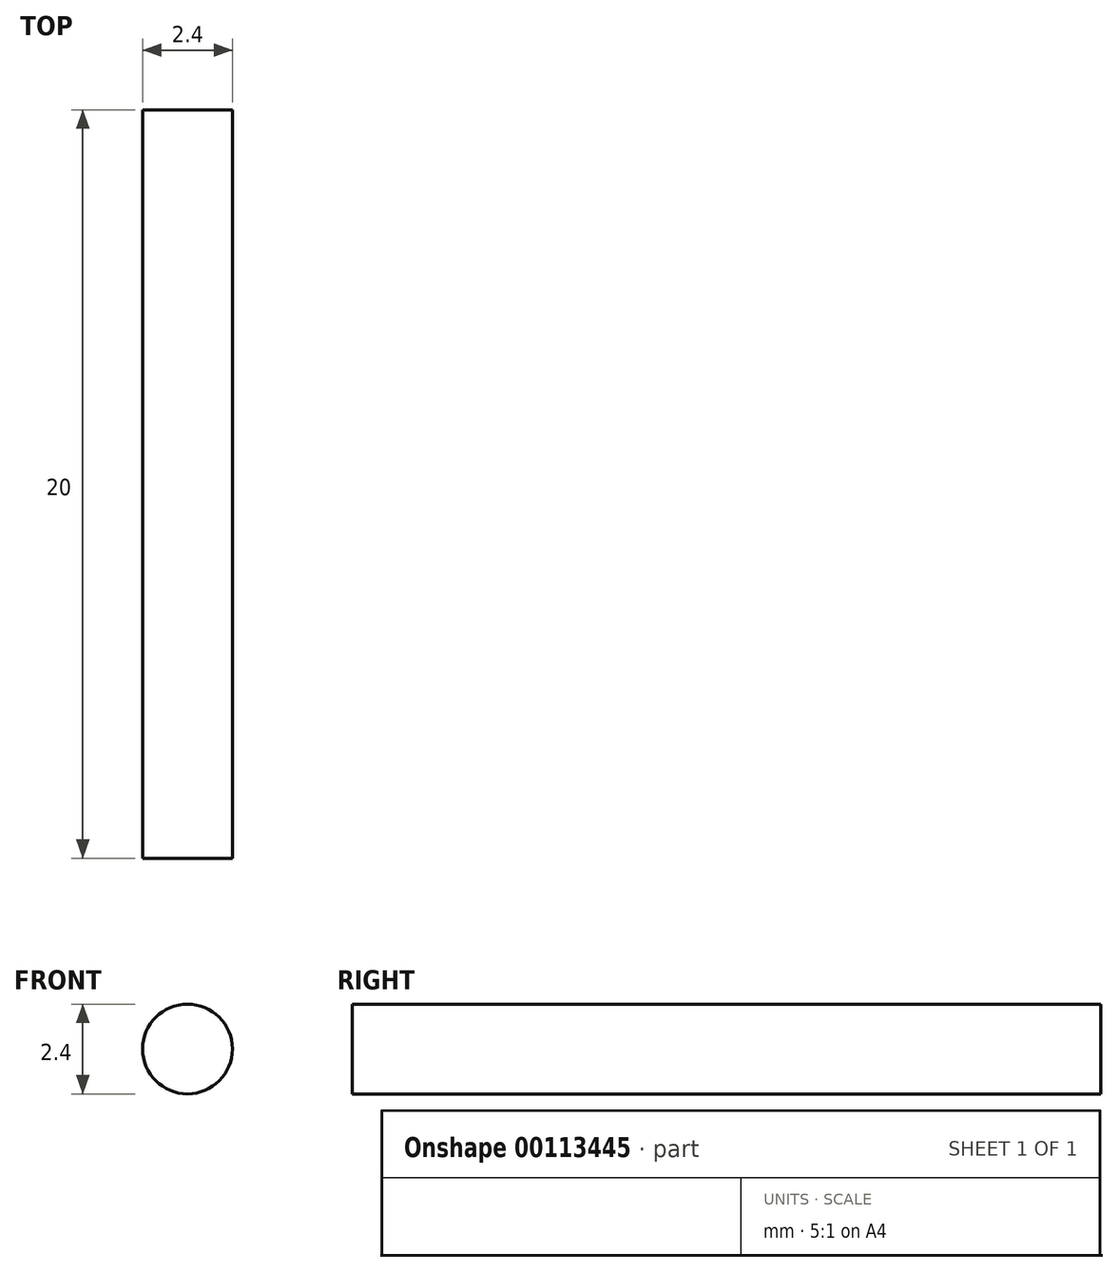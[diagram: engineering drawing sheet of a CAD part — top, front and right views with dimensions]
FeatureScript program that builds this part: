
annotation { "Feature Type Name" : "Feature", "Feature Type Description" : "" }
export const myFeature = defineFeature(function(context is Context, id is Id, definition is map)
    precondition{}
    {
        {
            var Q0;
            Q0=qCreatedBy(makeId("Front.planeOp"),FACE);
            var sketch = newSketch(context, id + "F0", { "sketchPlane" : qUnion([Q0])});
            skCircle(sketch, "E0", {"center": v(0, 0) * mm, "radius": 1.2 * mm});
            skSolve(sketch);
        }
        {
            var Q0;
            Q0 = qSketchRegion(id + "F0", true);
            extrude(context, id + "F1", {"entities" : qUnion([Q0]), "depth" : 20 * mm});
        }
    });
